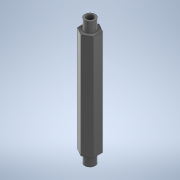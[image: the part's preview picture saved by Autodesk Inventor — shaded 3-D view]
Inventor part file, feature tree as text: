
AUTODESK INVENTOR PART (.ipt)
format: ipt  version: 2020 (Build 240168000, 168)  size: 137,216 bytes
history: native  units: in
note: dims shown in document units (in); Inventor stores cm internally (conversion verified against a paired STEP export)
features: extrude x3, sketch x3, projected_geometry x2
ambient origin geometry x8: Origin, YZ Plane, XZ Plane, XY Plane, X Axis, Y Axis, Z Axis, Center Point
bodies: Solid1 (feature_tree)
feature tree (8):
  extrude  "Extrusion1"  Depth=3.0in TaperAngle=0.0deg
  extrude  "Extrusion2"  Depth=0.25in TaperAngle=0.0deg
  extrude  "Extrusion3"  Depth=0.25in TaperAngle=0.0deg
  sketch  "Sketch1"  dims[d0=0.375in d1=3.0in d2=0.0in]
  sketch  "Sketch2"  dims[d3=0.25in d4=0.25in d5=0.0in]
  projected_geometry  "Projected Loop1"
  sketch  "Sketch3"  dims[d6=0.25in d7=0.25in d8=0.0in d9=0.165in]
  projected_geometry  "Projected Loop2"
